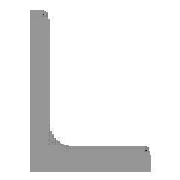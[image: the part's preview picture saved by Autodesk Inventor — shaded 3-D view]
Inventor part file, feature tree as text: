
AUTODESK INVENTOR PART (.ipt)
format: ipt  version: 2024.1 (Build 281209000, 209)  size: 120,832 bytes
history: native  units: mm (DEFAULTED — no unit token found)
features: other x4, sketch x1, plane x1
ambient origin geometry x8: Origin, YZ Plane, XZ Plane, XY Plane, X Axis, Y Axis, Z Axis, Center Point
bodies: Solid1 (feature_tree), Body (feature_tree)
feature tree (6):
  parser-record x1  (decoder bookkeeping rows leaked as tree rows — omitted from the tree; the rows remain in map.json)
  other  "Driven Length"
  other  "Start Plane"
  other  "End Plane"
  sketch  "Sketch3"  dims[d0=25.4mm d1=25.4mm d2=3.175mm d3=3.175mm d4=1200.0mm d5=0.0mm d10=0.0mm d11=0.0mm d12=-0.0mm d13=1200.0mm d14=3.302mm d15=1.524mm d16=90.0deg d17=1200.0mm]
  plane  "Work Plane3"
